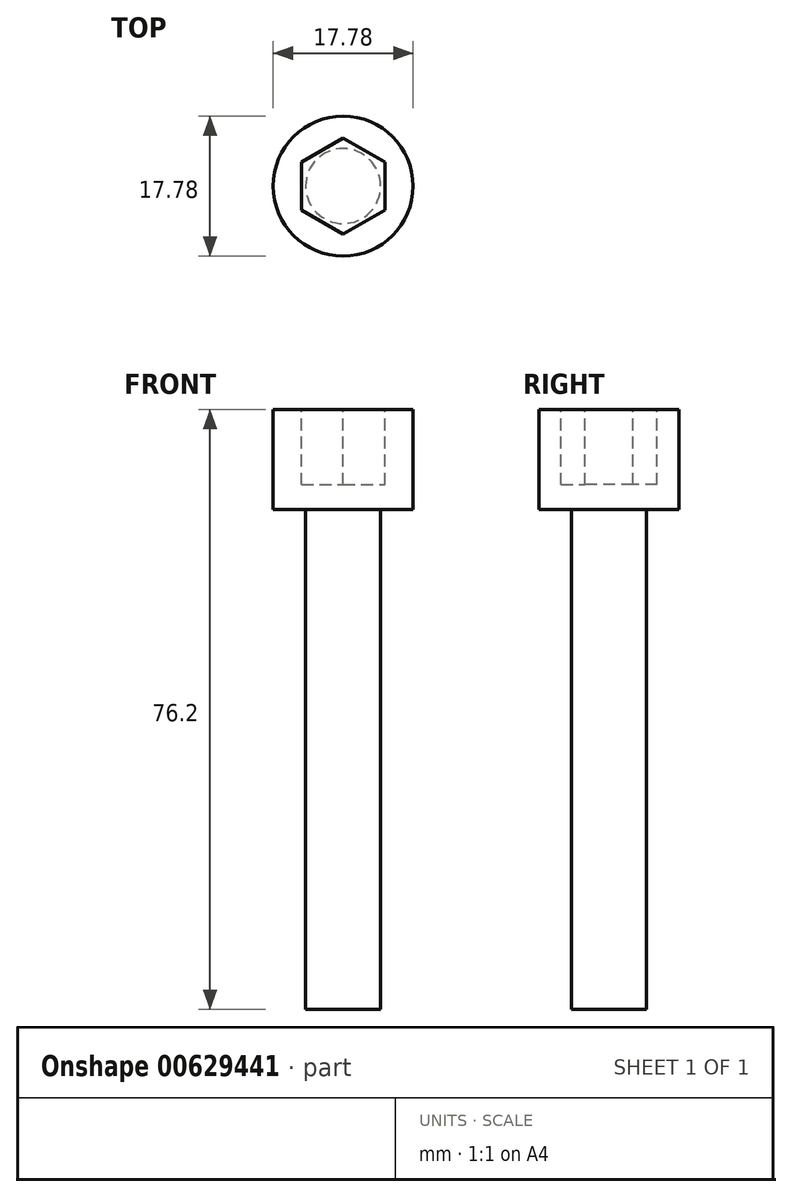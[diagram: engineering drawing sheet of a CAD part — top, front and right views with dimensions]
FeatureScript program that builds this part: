
annotation { "Feature Type Name" : "Feature", "Feature Type Description" : "" }
export const myFeature = defineFeature(function(context is Context, id is Id, definition is map)
    precondition{}
    {
        {
            var Q0;
            Q0=qCreatedBy(makeId("Top.planeOp"),FACE);
            var sketch = newSketch(context, id + "F0", { "sketchPlane" : qUnion([Q0])});
            skCircle(sketch, "E0", {"center": v(0, 0) * mm, "radius": 4.76 * mm});
            skSolve(sketch);
        }
        {
            var Q0;
            Q0=makeQuery(id+"F0.imprint","IMPRINT",FACE,{"disambiguationData":[TD([[makeQuery(id+"F0.imprint","IMPRINT",EDGE,{"derivedFrom":sQuery(id+"F0.wireOp",EDGE,"E0")}),1.0]])]});
            extrude(context, id + "F1", {"entities" : qUnion([Q0]), "oppositeDirection" : true, "depth" : 63.5 * mm, "offsetDistance" : 25.4 * mm});
        }
        {
            var Q0;
            Q0=qCreatedBy(makeId("Top.planeOp"),FACE);
            var sketch = newSketch(context, id + "F2", { "sketchPlane" : qUnion([Q0])});
            skCircle(sketch, "E1", {"center": v(0, 0) * mm, "radius": 8.9 * mm});
            skSolve(sketch);
        }
        {
            var Q0;
            Q0 = qSketchRegion(id + "F2", true);
            extrude(context, id + "F3", {"entities" : qUnion([Q0]), "operationType" : NewBodyOperationType.ADD, "depth" : 12.7 * mm, "offsetDistance" : 25.4 * mm});
        }
        {
            var Q0;
            Q0=makeQuery(id+"F3.opExtrude","CAP_FACE",FACE,{"disambiguationData":[OSD([sQuery(id+"F2.wireOp",EDGE,"E1")])],"isStart":false});
            var sketch = newSketch(context, id + "F4", { "sketchPlane" : qUnion([Q0])});
            skCircle(sketch, "E2.cCircle", {"center": v(0, 0) * mm, "radius": 5.3 * mm, "construction": true});
            skLineSegment(sketch, "E2.0", {"start": v(5.3, 3.06) * mm, "end": v(5.3, -3.06) * mm});
            skLineSegment(sketch, "E2.1", {"start": v(5.3, -3.06) * mm, "end": v(0, -6.11) * mm});
            skLineSegment(sketch, "E2.2", {"start": v(0, -6.11) * mm, "end": v(-5.3, -3.06) * mm});
            skLineSegment(sketch, "E2.3", {"start": v(-5.3, -3.06) * mm, "end": v(-5.3, 3.06) * mm});
            skLineSegment(sketch, "E2.4", {"start": v(-5.3, 3.06) * mm, "end": v(0, 6.11) * mm});
            skLineSegment(sketch, "E2.5", {"start": v(0, 6.11) * mm, "end": v(5.3, 3.06) * mm});
            skPoint(sketch, "E2.0.midPoint", {"position": v(5.3, 0) * mm});
            skSolve(sketch);
        }
        {
            var Q0;
            Q0=makeQuery(id+"F4.imprint","IMPRINT",FACE,{"disambiguationData":[TD([[makeQuery(id+"F4.imprint","IMPRINT",EDGE,{"derivedFrom":sQuery(id+"F4.wireOp",EDGE,"E2.0")}),-1.0]])]});
            extrude(context, id + "F5", {"entities" : qUnion([Q0]), "operationType" : NewBodyOperationType.REMOVE, "oppositeDirection" : true, "depth" : 9.54 * mm, "offsetDistance" : 25.4 * mm});
        }
    });
